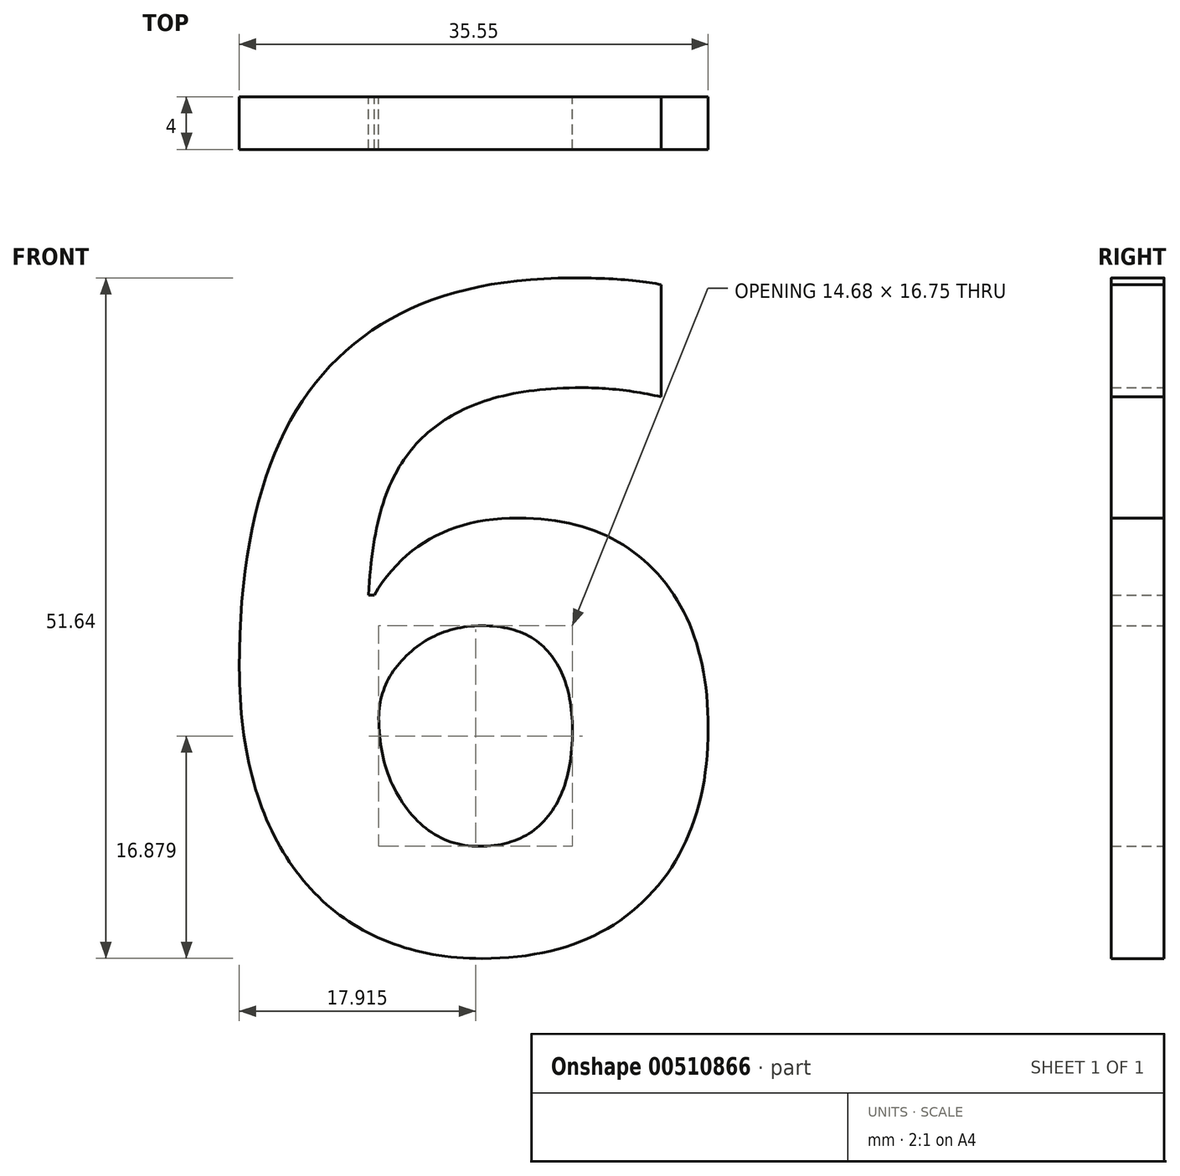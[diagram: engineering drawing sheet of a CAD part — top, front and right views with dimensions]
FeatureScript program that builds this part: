
annotation { "Feature Type Name" : "Feature", "Feature Type Description" : "" }
export const myFeature = defineFeature(function(context is Context, id is Id, definition is map)
    precondition{}
    {
        {
            var Q0;
            Q0=qCreatedBy(makeId("Front.planeOp"),FACE);
            var sketch = newSketch(context, id + "F0", { "sketchPlane" : qUnion([Q0])});
            skText(sketch, "E0", { "text": "6", "fontName": "OpenSans-Bold.ttf"});
            const initialGuessF0  = {"E0": [0, 0, 1, 0, 0.0508]};
            skSetInitialGuess(sketch, initialGuessF0);
            skSolve(sketch);
        }
        {
            var Q0;
            Q0=makeQuery(id+"F0.imprint","IMPRINT",FACE,{"disambiguationData":[TD([[makeQuery(id+"F0.imprint","IMPRINT",EDGE,{"derivedFrom":sQuery(id+"F0.wireOp",EDGE,"E0.sketch_text.stroke-0")}),-1.0]])]});
            extrude(context, id + "F1", {"entities" : qUnion([Q0]), "depth" : 4 * mm});
        }
    });
